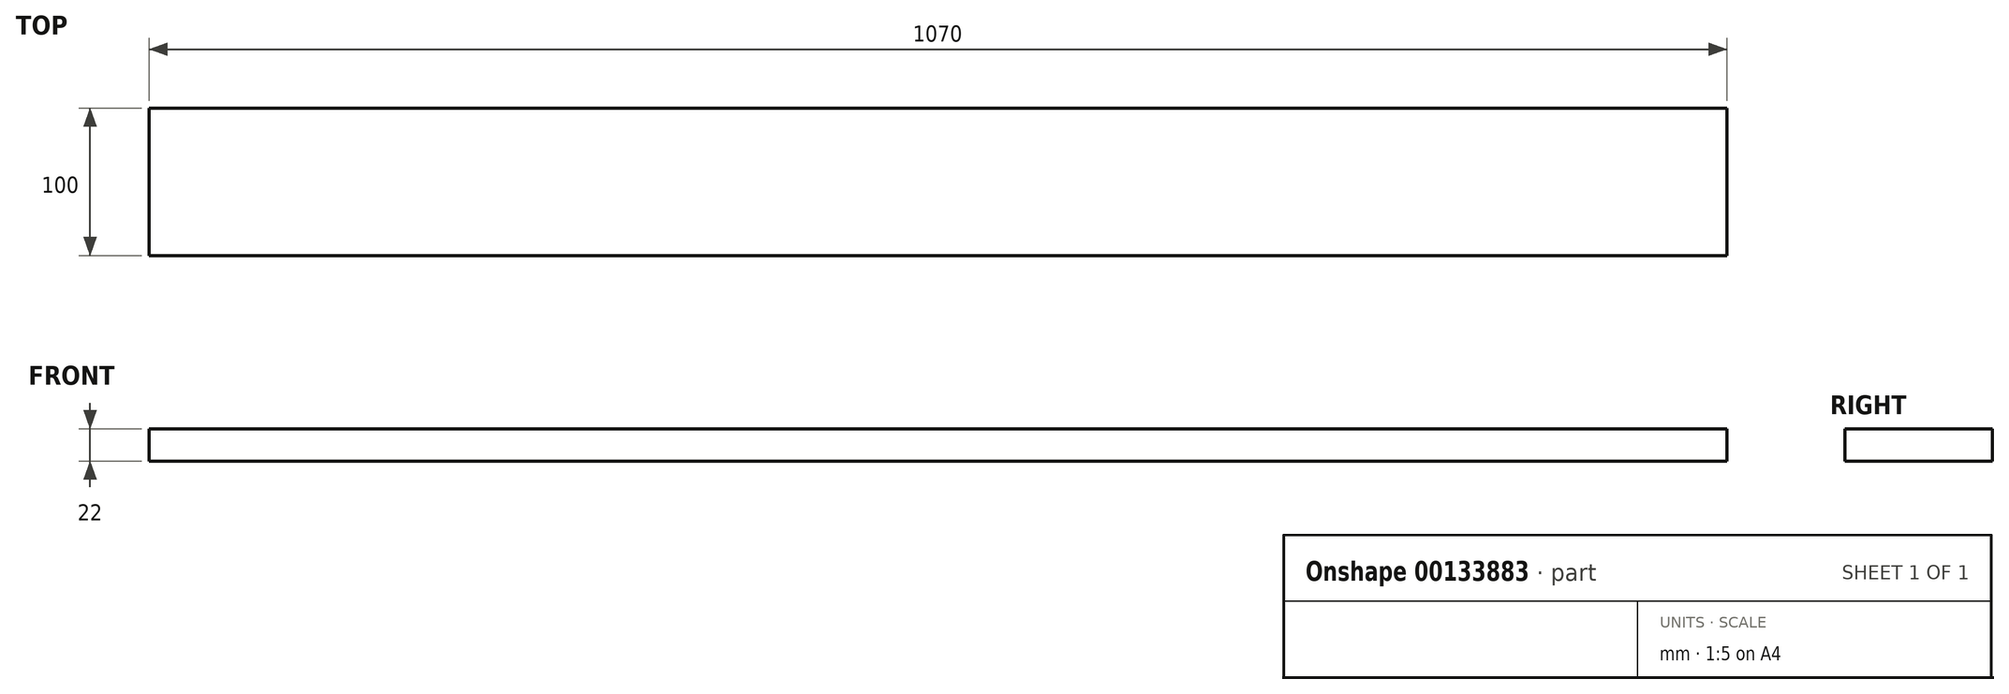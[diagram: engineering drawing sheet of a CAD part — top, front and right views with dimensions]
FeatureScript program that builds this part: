
annotation { "Feature Type Name" : "Feature", "Feature Type Description" : "" }
export const myFeature = defineFeature(function(context is Context, id is Id, definition is map)
    precondition{}
    {
        {
            assignVariable(context, id + "F0", {"name" : "Staerke", "anyValue" : 22 * mm});
        }
        {
            var Q0;
            Q0=qCreatedBy(makeId("Top.planeOp"),FACE);
            var sketch = newSketch(context, id + "F1", { "sketchPlane" : qUnion([Q0])});
            skLineSegment(sketch, "E0.bottom", {"start": v(-535, 50) * mm, "end": v(535, 50) * mm});
            skLineSegment(sketch, "E0.top", {"start": v(-535, -50) * mm, "end": v(535, -50) * mm});
            skLineSegment(sketch, "E0.left", {"start": v(-535, 50) * mm, "end": v(-535, -50) * mm});
            skLineSegment(sketch, "E0.right", {"start": v(535, 50) * mm, "end": v(535, -50) * mm});
            skLineSegment(sketch, "E1", {"start": v(0, 50) * mm, "end": v(0, 0) * mm, "construction": true});
            skPoint(sketch, "E1.endSnap0", {"position": v(535, 0) * mm});
            skLineSegment(sketch, "E2", {"start": v(0, 0) * mm, "end": v(535, 0) * mm, "construction": true});
            skSolve(sketch);
        }
        {
            var Q0;
            Q0 = qSketchRegion(id + "F1", true);
            var Q1;
            Q1=makeQuery(id+"F1.imprint","IMPRINT",FACE,{"disambiguationData":[TD([[makeQuery(id+"F1.imprint","IMPRINT",EDGE,{"derivedFrom":sQuery(id+"F1.wireOp",EDGE,"E0.bottom")}),-1.0]])]});
            extrude(context, id + "F2", {"entities" : qUnion([Q0, Q1]), "depth" : getVariable(context, 'Staerke')});
        }
    });
